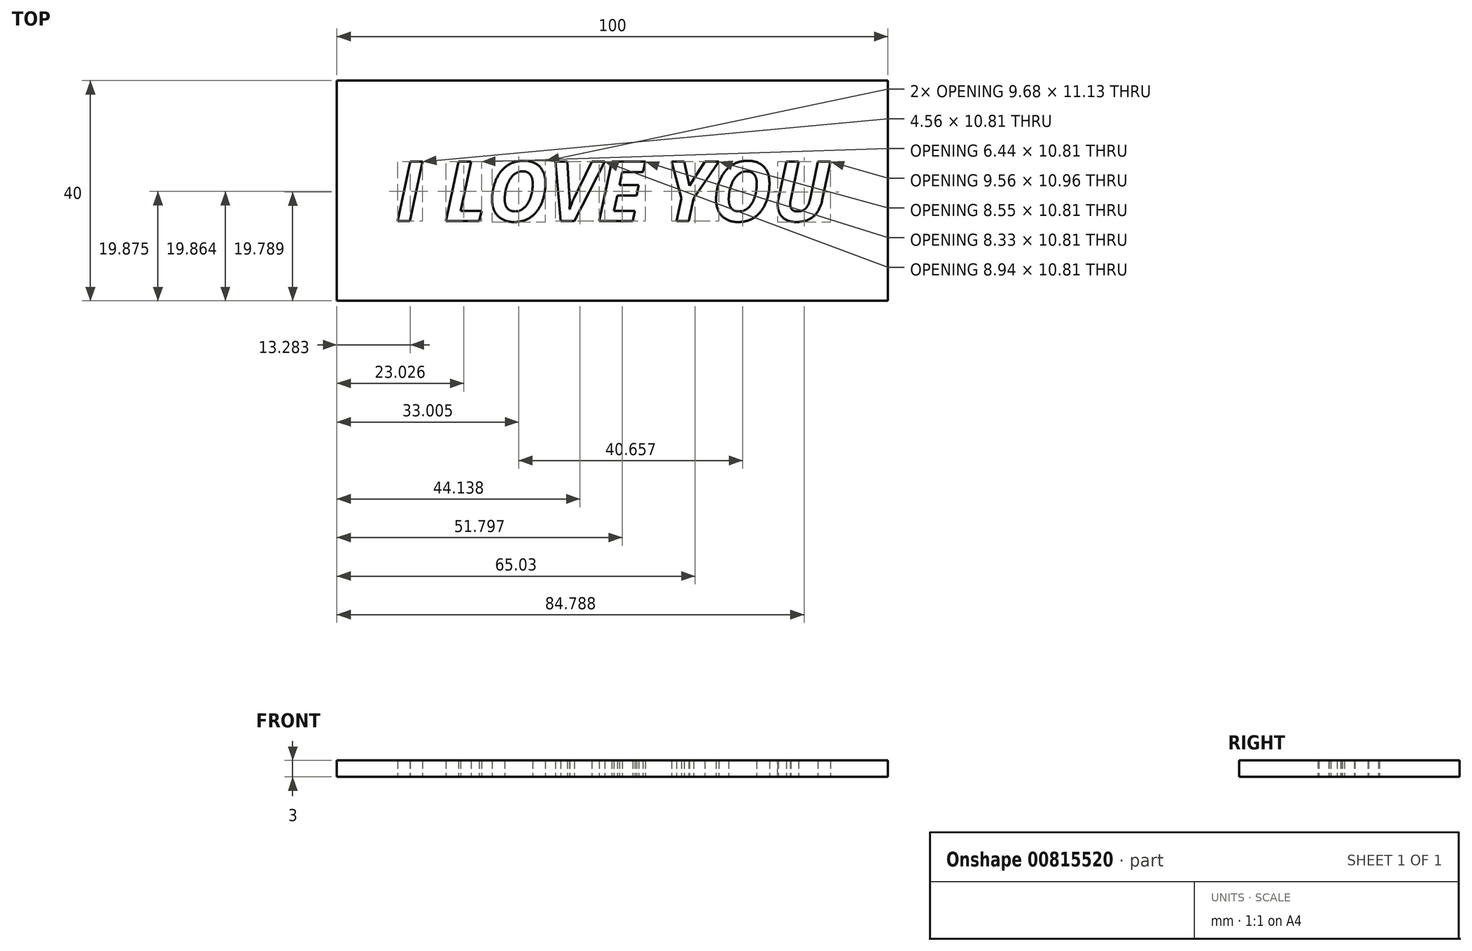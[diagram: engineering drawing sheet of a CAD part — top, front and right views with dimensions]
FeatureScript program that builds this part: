
annotation { "Feature Type Name" : "Feature", "Feature Type Description" : "" }
export const myFeature = defineFeature(function(context is Context, id is Id, definition is map)
    precondition{}
    {
        {
            var Q0;
            Q0=qCreatedBy(makeId("Top.planeOp"),FACE);
            var sketch = newSketch(context, id + "F0", { "sketchPlane" : qUnion([Q0])});
            skLineSegment(sketch, "E0.bottom", {"start": v(-50, 20) * mm, "end": v(50, 20) * mm});
            skLineSegment(sketch, "E0.top", {"start": v(-50, -20) * mm, "end": v(50, -20) * mm});
            skLineSegment(sketch, "E0.left", {"start": v(-50, 20) * mm, "end": v(-50, -20) * mm});
            skLineSegment(sketch, "E0.right", {"start": v(50, 20) * mm, "end": v(50, -20) * mm});
            skPoint(sketch, "E0.middle", {"position": v(0, 0) * mm});
            skText(sketch, "E1", { "text": "I LOVE YOU", "fontName": "OpenSans-BoldItalic.ttf"});
            const initialGuessF0  = {"E1": [-0.03939, -0.00554, 1, 0, 0.0109]};
            skSetInitialGuess(sketch, initialGuessF0);
            skSolve(sketch);
        }
        {
            var Q0;
            Q0=makeQuery(id+"F0.imprint","IMPRINT",FACE,{"disambiguationData":[TD([[makeQuery(id+"F0.imprint","IMPRINT",EDGE,{"derivedFrom":sQuery(id+"F0.wireOp",EDGE,"E1.sketch_text.stroke-20")}),1.0]])]});
            var Q1;
            Q1=makeQuery(id+"F0.imprint","IMPRINT",FACE,{"disambiguationData":[TD([[makeQuery(id+"F0.imprint","IMPRINT",EDGE,{"derivedFrom":sQuery(id+"F0.wireOp",EDGE,"E1.sketch_text.stroke-72")}),1.0]])]});
            var Q2;
            Q2=makeQuery(id+"F0.imprint","IMPRINT",FACE,{"disambiguationData":[TD([[makeQuery(id+"F0.imprint","IMPRINT",EDGE,{"derivedFrom":sQuery(id+"F0.wireOp",EDGE,"E0.bottom")}),-1.0]])]});
            extrude(context, id + "F1", {"entities" : qUnion([Q0, Q1, Q2]), "depth" : 3 * mm, "offsetDistance" : 25 * mm});
        }
    });
